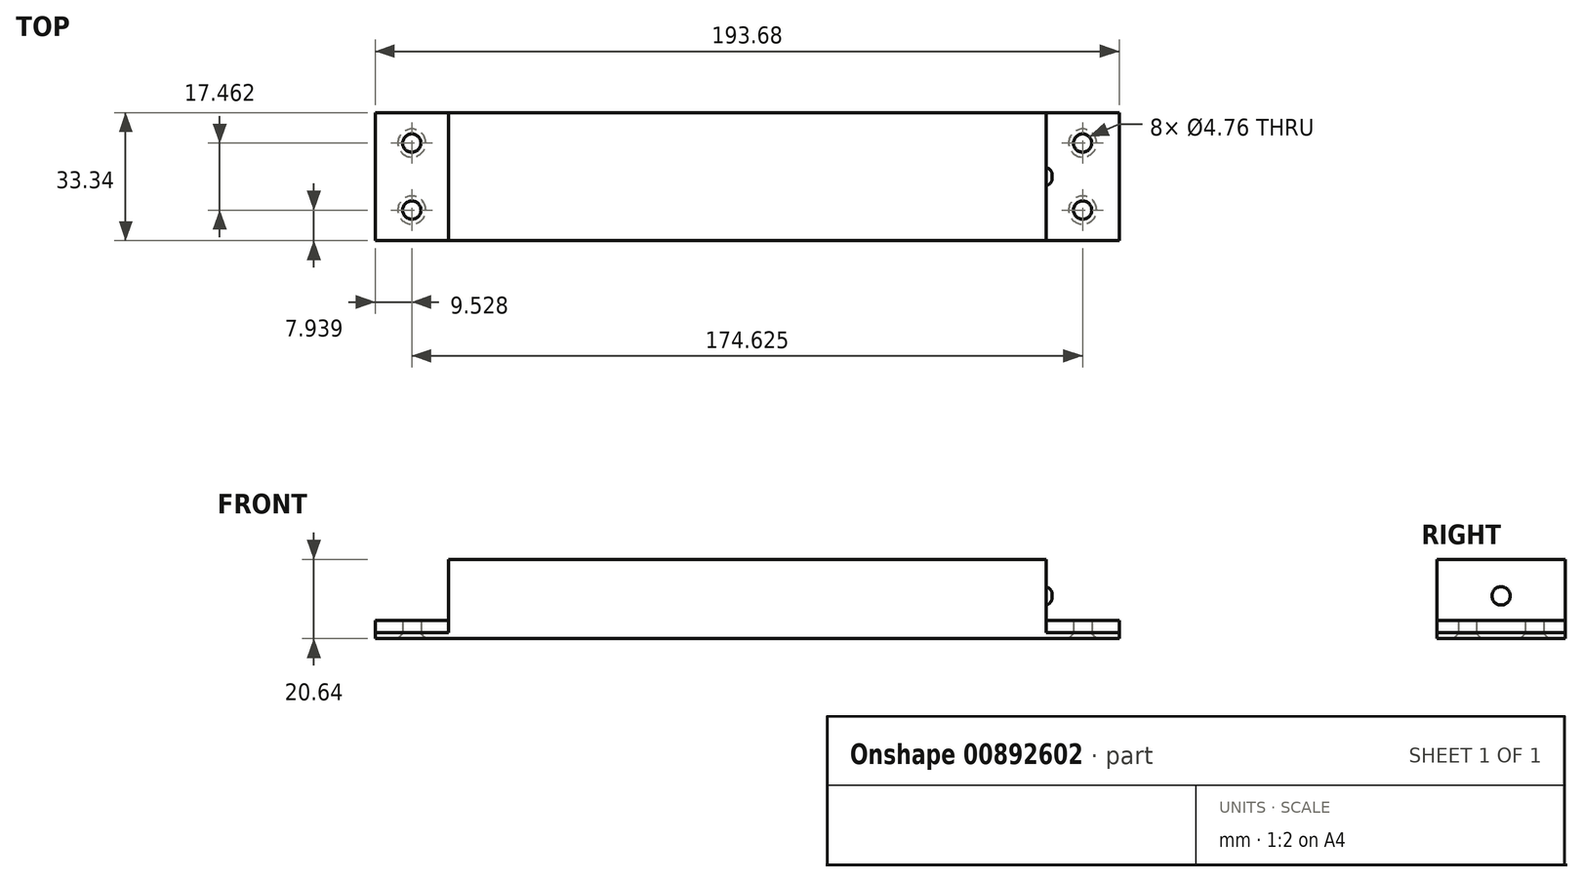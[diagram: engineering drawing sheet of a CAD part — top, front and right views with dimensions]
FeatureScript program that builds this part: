
annotation { "Feature Type Name" : "Feature", "Feature Type Description" : "" }
export const myFeature = defineFeature(function(context is Context, id is Id, definition is map)
    precondition{}
    {
        {
            var Q0;
            Q0=qCreatedBy(makeId("Top.planeOp"),FACE);
            var sketch = newSketch(context, id + "F0", { "sketchPlane" : qUnion([Q0])});
            skPoint(sketch, "E0.middle", {"position": v(0, 0) * mm});
            skLineSegment(sketch, "E1.bottom", {"start": v(-96.84, 16.67) * mm, "end": v(96.84, 16.67) * mm});
            skLineSegment(sketch, "E1.top", {"start": v(-96.84, -16.67) * mm, "end": v(96.84, -16.67) * mm});
            skLineSegment(sketch, "E1.left", {"start": v(-96.84, 16.67) * mm, "end": v(-96.84, -16.67) * mm});
            skLineSegment(sketch, "E1.right", {"start": v(96.84, 16.67) * mm, "end": v(96.84, -16.67) * mm});
            skLineSegment(sketch, "E2", {"start": v(-77.79, 16.67) * mm, "end": v(-77.79, -16.67) * mm});
            skLineSegment(sketch, "E3", {"start": v(77.79, 16.67) * mm, "end": v(77.79, -16.67) * mm});
            skCircle(sketch, "E4", {"center": v(-87.31, 8.73) * mm, "radius": 2.38 * mm});
            skCircle(sketch, "E5", {"center": v(-87.31, -8.73) * mm, "radius": 2.38 * mm});
            skCircle(sketch, "E6.MirrorC", {"center": v(87.31, -8.73) * mm, "radius": 2.38 * mm});
            skCircle(sketch, "E7.MirrorC", {"center": v(87.31, 8.73) * mm, "radius": 2.38 * mm});
            skSolve(sketch);
        }
        {
            var Q0;
            {var subQ0=sQuery(id+"F0.wireOp",EDGE,"E2");Q0=makeQuery(id+"F0.imprint","IMPRINT",FACE,{"disambiguationData":[TD([[makeQuery(id+"F0.imprint","IMPRINT",EDGE,{"derivedFrom":subQ0}),1.0]])]});}
            extrude(context, id + "F1", {"entities" : qUnion([Q0]), "depth" : 20.64 * mm, "offsetDistance" : 25.4 * mm});
        }
        {
            var Q0;
            {var subQ0=sQuery(id+"F0.wireOp",EDGE,"E1.left");Q0=makeQuery(id+"F0.imprint","IMPRINT",FACE,{"disambiguationData":[TD([[makeQuery(id+"F0.imprint","IMPRINT",EDGE,{"derivedFrom":subQ0}),1.0]])]});}
            var Q1;
            {var subQ1=sQuery(id+"F0.wireOp",EDGE,"E1.right");Q1=makeQuery(id+"F0.imprint","IMPRINT",FACE,{"disambiguationData":[TD([[makeQuery(id+"F0.imprint","IMPRINT",EDGE,{"derivedFrom":subQ1}),-1.0]])]});}
            extrude(context, id + "F2", {"entities" : qUnion([Q0, Q1]), "operationType" : NewBodyOperationType.ADD, "depth" : 1.59 * mm, "offsetDistance" : 25.4 * mm});
        }
        {
            var Q0;
            Q0=makeQuery(id+"F2.opExtrude","CAP_EDGE",EDGE,{"disambiguationData":[OSD([sQuery(id+"F0.wireOp",EDGE,"E5")])],"isStart":true});
            var Q1;
            Q1=makeQuery(id+"F2.opExtrude","CAP_EDGE",EDGE,{"disambiguationData":[OSD([sQuery(id+"F0.wireOp",EDGE,"E4")])],"isStart":true});
            var Q2;
            Q2=makeQuery(id+"F2.opExtrude","CAP_EDGE",EDGE,{"disambiguationData":[OSD([sQuery(id+"F0.wireOp",EDGE,"E6.MirrorC")])],"isStart":true});
            var Q3;
            Q3=makeQuery(id+"F2.opExtrude","CAP_EDGE",EDGE,{"disambiguationData":[OSD([sQuery(id+"F0.wireOp",EDGE,"E7.MirrorC")])],"isStart":true});
            chamfer(context, id + "F3", {"entities" : qUnion([Q0, Q1, Q2, Q3]), "width" : 1.27 * mm, "tangentPropagation" : true});
        }
        {
            var Q0;
            Q0=makeQuery(id+"F1.opExtrude","SWEPT_FACE",FACE,{"disambiguationData":[OSD([sQuery(id+"F0.wireOp",EDGE,"E3")])]});
            var sketch = newSketch(context, id + "F4", { "sketchPlane" : qUnion([Q0])});
            skCircle(sketch, "E8", {"center": v(0, 11.11) * mm, "radius": 2.38 * mm});
            skPoint(sketch, "E8.centerSnap0", {"position": v(-16.67, 11.11) * mm});
            skPoint(sketch, "E8.centerSnap1", {"position": v(0, 1.59) * mm});
            skSolve(sketch);
        }
        {
            var Q0;
            Q0 = qSketchRegion(id + "F4", true);
            extrude(context, id + "F5", {"entities" : qUnion([Q0]), "operationType" : NewBodyOperationType.ADD, "depth" : 1.59 * mm, "offsetDistance" : 25.4 * mm});
        }
        {
            var Q0;
            Q0=makeQuery(id+"F5.opExtrude","CAP_EDGE",EDGE,{"disambiguationData":[OSD([sQuery(id+"F4.wireOp",EDGE,"E8")])],"isStart":false});
            fillet(context, id + "F6", {"entities" : qUnion([Q0]), "radius" : 2.03 * mm, "tangentPropagation" : true, "allowEdgeOverflow" : false});
        }
        {
            var Q0;
            Q0=makeQuery(id+"F2.opExtrude","CAP_FACE",FACE,{"disambiguationData":[OSD([sQuery(id+"F0.wireOp",EDGE,"E1.bottom"),sQuery(id+"F0.wireOp",EDGE,"E1.top"),sQuery(id+"F0.wireOp",EDGE,"E1.left"),sQuery(id+"F0.wireOp",EDGE,"E2"),sQuery(id+"F0.wireOp",EDGE,"E4"),sQuery(id+"F0.wireOp",EDGE,"E5")])],"isStart":false});
            var Q1;
            Q1=makeQuery(id+"F2.opExtrude","CAP_FACE",FACE,{"disambiguationData":[OSD([sQuery(id+"F0.wireOp",EDGE,"E1.bottom"),sQuery(id+"F0.wireOp",EDGE,"E1.top"),sQuery(id+"F0.wireOp",EDGE,"E1.right"),sQuery(id+"F0.wireOp",EDGE,"E3"),sQuery(id+"F0.wireOp",EDGE,"E6.MirrorC"),sQuery(id+"F0.wireOp",EDGE,"E7.MirrorC")])],"isStart":false});
            extrude(context, id + "F7", {"entities" : qUnion([Q0, Q1]), "depth" : 3.17 * mm, "offsetDistance" : 25.4 * mm});
        }
    });
